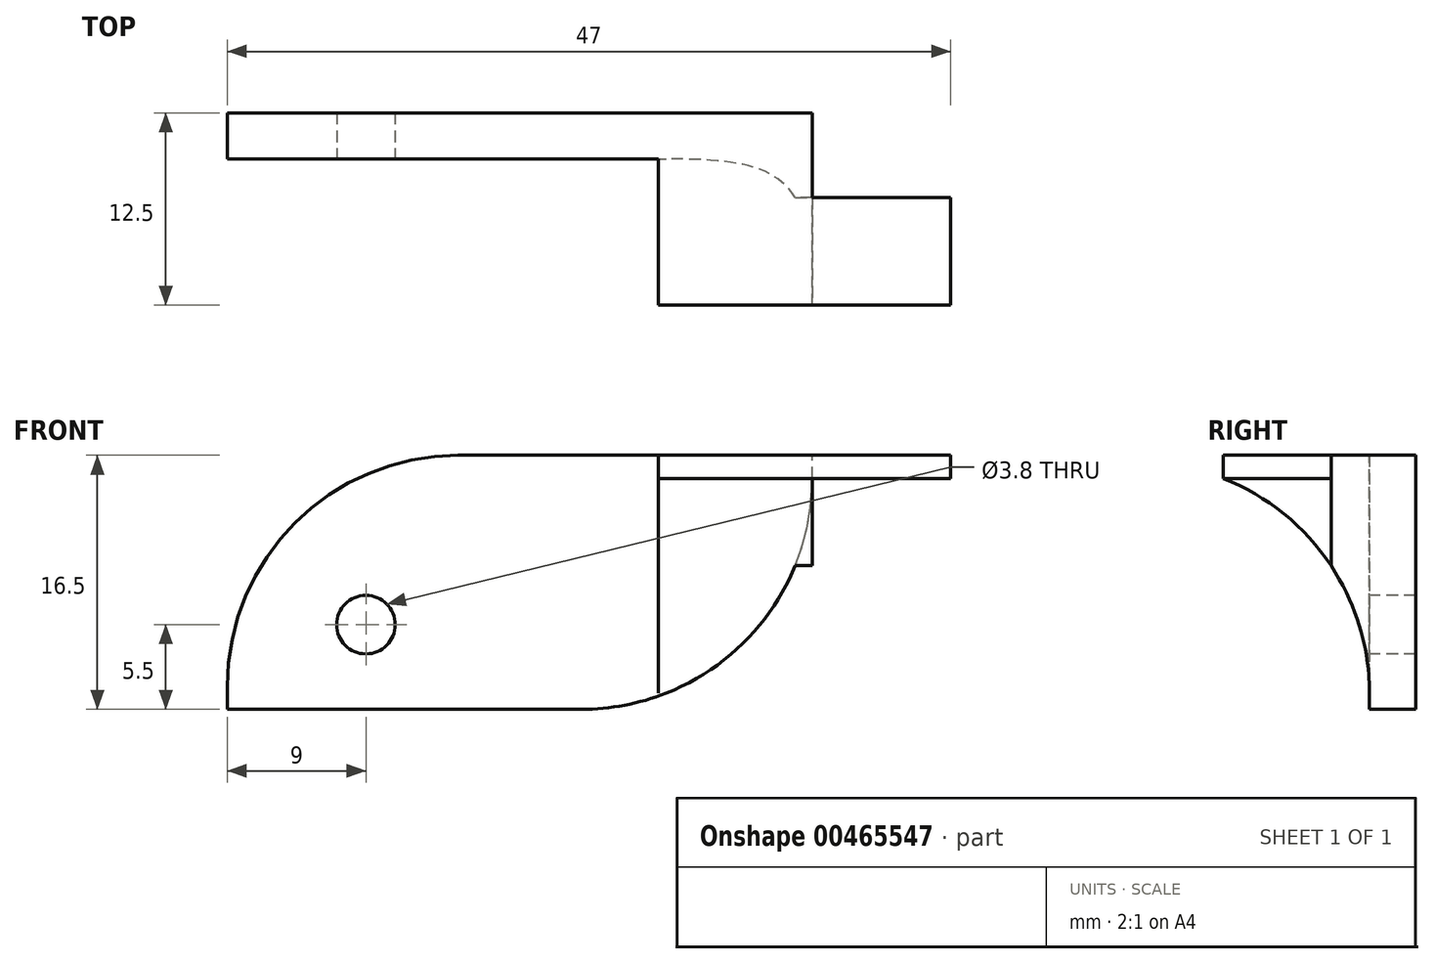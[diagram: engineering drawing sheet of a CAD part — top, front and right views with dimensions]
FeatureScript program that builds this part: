
annotation { "Feature Type Name" : "Feature", "Feature Type Description" : "" }
export const myFeature = defineFeature(function(context is Context, id is Id, definition is map)
    precondition{}
    {
        {
            var Q0;
            Q0=qCreatedBy(makeId("Front.planeOp"),FACE);
            var sketch = newSketch(context, id + "F0", { "sketchPlane" : qUnion([Q0])});
            skLineSegment(sketch, "E0.bottom", {"start": v(0, 0) * mm, "end": v(-38, 0) * mm});
            skLineSegment(sketch, "E0.top", {"start": v(0, 16.5) * mm, "end": v(-38, 16.5) * mm});
            skLineSegment(sketch, "E0.left", {"start": v(0, 0) * mm, "end": v(0, 16.5) * mm});
            skLineSegment(sketch, "E0.right", {"start": v(-38, 0) * mm, "end": v(-38, 16.5) * mm});
            skSolve(sketch);
        }
        {
            var Q0;
            Q0=makeQuery(id+"F0.imprint","IMPRINT",FACE,{"disambiguationData":[TD([[makeQuery(id+"F0.imprint","IMPRINT",EDGE,{"derivedFrom":sQuery(id+"F0.wireOp",EDGE,"E0.bottom")}),-1.0]])]});
            extrude(context, id + "F1", {"entities" : qUnion([Q0]), "oppositeDirection" : true, "depth" : 3 * mm});
        }
        {
            var Q0;
            Q0=makeQuery(id+"F1.opExtrude","SWEPT_FACE",FACE,{"disambiguationData":[OSD([sQuery(id+"F0.wireOp",EDGE,"E0.top")])]});
            var sketch = newSketch(context, id + "F2", { "sketchPlane" : qUnion([Q0])});
            skLineSegment(sketch, "E1", {"start": v(0, 3) * mm, "end": v(0, -2.5) * mm});
            skLineSegment(sketch, "E2", {"start": v(0, -2.5) * mm, "end": v(9, -2.5) * mm});
            skLineSegment(sketch, "E3", {"start": v(9, -2.5) * mm, "end": v(9, -9.5) * mm});
            skLineSegment(sketch, "E4", {"start": v(9, -9.5) * mm, "end": v(-10, -9.5) * mm});
            skLineSegment(sketch, "E5", {"start": v(-10, -9.5) * mm, "end": v(-10, 3) * mm});
            skLineSegment(sketch, "E6", {"start": v(-10, 3) * mm, "end": v(0, 3) * mm});
            skSolve(sketch);
        }
        {
            var Q0;
            Q0 = qSketchRegion(id + "F2", true);
            extrude(context, id + "F3", {"entities" : qUnion([Q0]), "operationType" : NewBodyOperationType.ADD, "oppositeDirection" : true, "depth" : 1.5 * mm});
        }
        {
            var Q0;
            Q0=qCreatedBy(makeId("Front.planeOp"),FACE);
            var sketch = newSketch(context, id + "F4", { "sketchPlane" : qUnion([Q0])});
            skPoint(sketch, "E7", {"position": v(-29, 5.5) * mm});
            skSolve(sketch);
        }
        {
            var Q0;
            Q0=sQuery(id+"F4.wireOp",VERTEX,"E7");
            var Q1;
            Q1=makeQuery(id+"F1.opExtrude","SWEPT_BODY",BODY,{"disambiguationData":[OSD([sQuery(id+"F0.wireOp",EDGE,"E0.bottom"),sQuery(id+"F0.wireOp",EDGE,"E0.top"),sQuery(id+"F0.wireOp",EDGE,"E0.left"),sQuery(id+"F0.wireOp",EDGE,"E0.right")])]});
            hole(context, id + "F5", {"style" : HoleStyle.SIMPLE, "endStyle" : HoleEndStyle.THROUGH, "holeDiameter" : 3.8 * mm, "tappedDepth" : 12 * mm, "tapClearance" : 3, "locations" : qUnion([Q0]), "scope" : qUnion([Q1])});
        }
        {
            var Q0;
            Q0=makeQuery(id+"F1.opExtrude","SWEPT_EDGE",EDGE,{"disambiguationData":[OSD([sQuery(id+"F0.wireOp",EDGE,"E0.top"),sQuery(id+"F0.wireOp",EDGE,"E0.right")])]});
            fillet(context, id + "F6", {"entities" : qUnion([Q0]), "radius" : 15 * mm, "tangentPropagation" : true, "allowEdgeOverflow" : false});
        }
        {
            var Q0;
            Q0=qCreatedBy(makeId("Front.planeOp"),FACE);
            var sketch = newSketch(context, id + "F7", { "sketchPlane" : qUnion([Q0])});
            skLineSegment(sketch, "E8.bottom", {"start": v(0, 15) * mm, "end": v(9, 15) * mm});
            skLineSegment(sketch, "E8.top", {"start": v(0, 0) * mm, "end": v(9, 0) * mm});
            skLineSegment(sketch, "E8.left", {"start": v(0, 15) * mm, "end": v(0, 0) * mm});
            skLineSegment(sketch, "E8.right", {"start": v(9, 15) * mm, "end": v(9, 0) * mm});
            skSolve(sketch);
        }
        {
            var Q0;
            Q0=makeQuery(id+"FiQzaQvZ3gbE16m_1.boolean.opBoolean","MERGE",EDGE,{"derivedFrom":[makeQuery(id+"F1.opExtrude","SWEPT_EDGE",EDGE,{"disambiguationData":[OSD([sQuery(id+"F0.wireOp",EDGE,"E0.bottom"),sQuery(id+"F0.wireOp",EDGE,"E0.left")])]}),makeQuery(id+"FiQzaQvZ3gbE16m_1.opExtrude","SWEPT_EDGE",EDGE,{"disambiguationData":[OSD([sQuery(id+"FXEPKCIM568FOeN_1.wireOp",EDGE,"idCmTC15-okho-4DaV-Lm5P-D4V3eyssAwB4.bottom"),sQuery(id+"FXEPKCIM568FOeN_1.wireOp",EDGE,"idCmTC15-okho-4DaV-Lm5P-D4V3eyssAwB4.right")])]})]});
            fillet(context, id + "F8", {"entities" : qUnion([Q0]), "radius" : 15 * mm, "tangentPropagation" : true, "allowEdgeOverflow" : false});
        }
        {
            var Q0;
            Q0=makeQuery(id+"F3.boolean.opBoolean","INTERSECT",EDGE,{"derivedFrom":[makeQuery(id+"F1.opExtrude","CAP_FACE",FACE,{"disambiguationData":[OSD([sQuery(id+"F0.wireOp",EDGE,"E0.bottom"),sQuery(id+"F0.wireOp",EDGE,"E0.top"),sQuery(id+"F0.wireOp",EDGE,"E0.left"),sQuery(id+"F0.wireOp",EDGE,"E0.right")])],"isStart":true}),makeQuery(id+"F3.opExtrude","CAP_FACE",FACE,{"disambiguationData":[OSD([sQuery(id+"F2.wireOp",EDGE,"E1"),sQuery(id+"F2.wireOp",EDGE,"E2"),sQuery(id+"F2.wireOp",EDGE,"E3"),sQuery(id+"F2.wireOp",EDGE,"E4"),sQuery(id+"F2.wireOp",EDGE,"E5"),sQuery(id+"F2.wireOp",EDGE,"E6")])],"isStart":false})]});
            fillet(context, id + "F9", {"entities" : qUnion([Q0]), "radius" : 15 * mm, "tangentPropagation" : true, "allowEdgeOverflow" : false});
        }
        {
            var Q0;
            Q0=makeQuery(id+"F7.imprint","IMPRINT",FACE,{"disambiguationData":[TD([[makeQuery(id+"F7.imprint","IMPRINT",EDGE,{"derivedFrom":sQuery(id+"F7.wireOp",EDGE,"E8.bottom")}),-1.0]])]});
            extrude(context, id + "F10", {"entities" : qUnion([Q0]), "operationType" : NewBodyOperationType.REMOVE, "depth" : 25 * mm});
        }
    });
